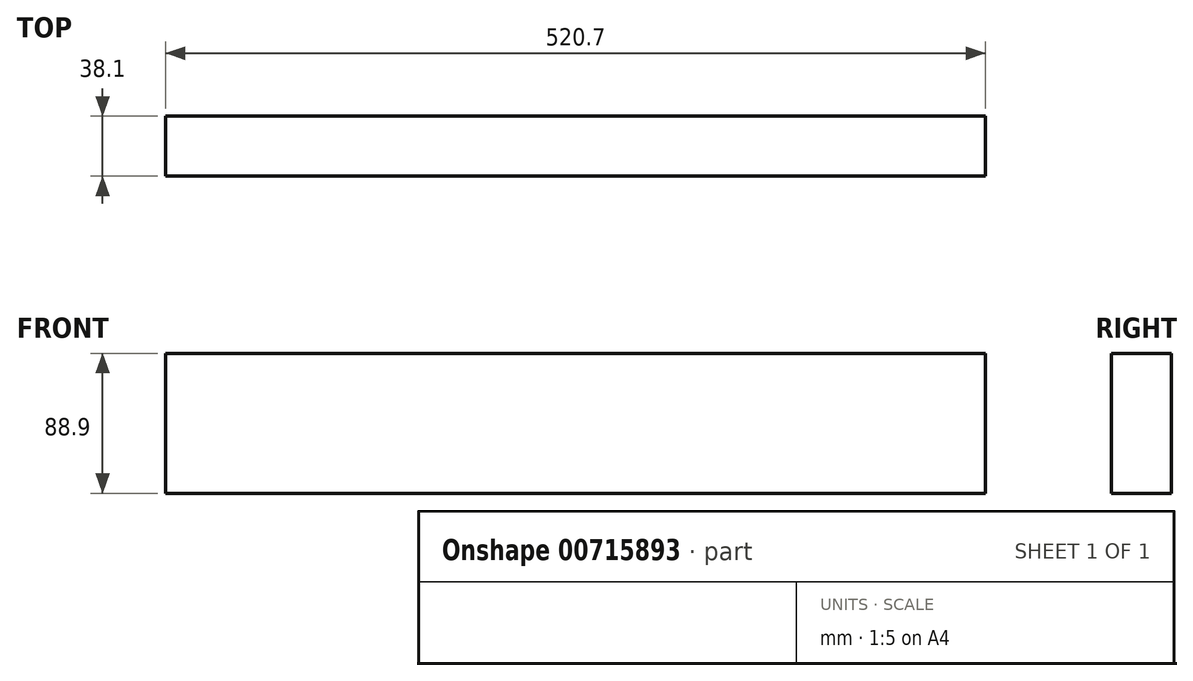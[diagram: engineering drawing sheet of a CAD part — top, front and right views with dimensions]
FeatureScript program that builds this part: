
annotation { "Feature Type Name" : "Feature", "Feature Type Description" : "" }
export const myFeature = defineFeature(function(context is Context, id is Id, definition is map)
    precondition{}
    {
        {
            var Q0;
            Q0=qCreatedBy(makeId("Right.planeOp"),FACE);
            var sketch = newSketch(context, id + "F0", { "sketchPlane" : qUnion([Q0])});
            skLineSegment(sketch, "E0.bottom", {"start": v(-19.05, 44.45) * mm, "end": v(19.05, 44.45) * mm});
            skLineSegment(sketch, "E0.top", {"start": v(-19.05, -44.45) * mm, "end": v(19.05, -44.45) * mm});
            skLineSegment(sketch, "E0.left", {"start": v(-19.05, 44.45) * mm, "end": v(-19.05, -44.45) * mm});
            skLineSegment(sketch, "E0.right", {"start": v(19.05, 44.45) * mm, "end": v(19.05, -44.45) * mm});
            skPoint(sketch, "E0.middle", {"position": v(0, 0) * mm});
            skSolve(sketch);
        }
        {
            var Q0;
            Q0=makeQuery(id+"F0.imprint","IMPRINT",FACE,{"disambiguationData":[TD([[makeQuery(id+"F0.imprint","IMPRINT",EDGE,{"derivedFrom":sQuery(id+"F0.wireOp",EDGE,"E0.bottom")}),-1.0]])]});
            extrude(context, id + "F1", {"entities" : qUnion([Q0]), "depth" : 520.7 * mm, "offsetDistance" : 25.4 * mm, "symmetric" : true});
        }
    });
